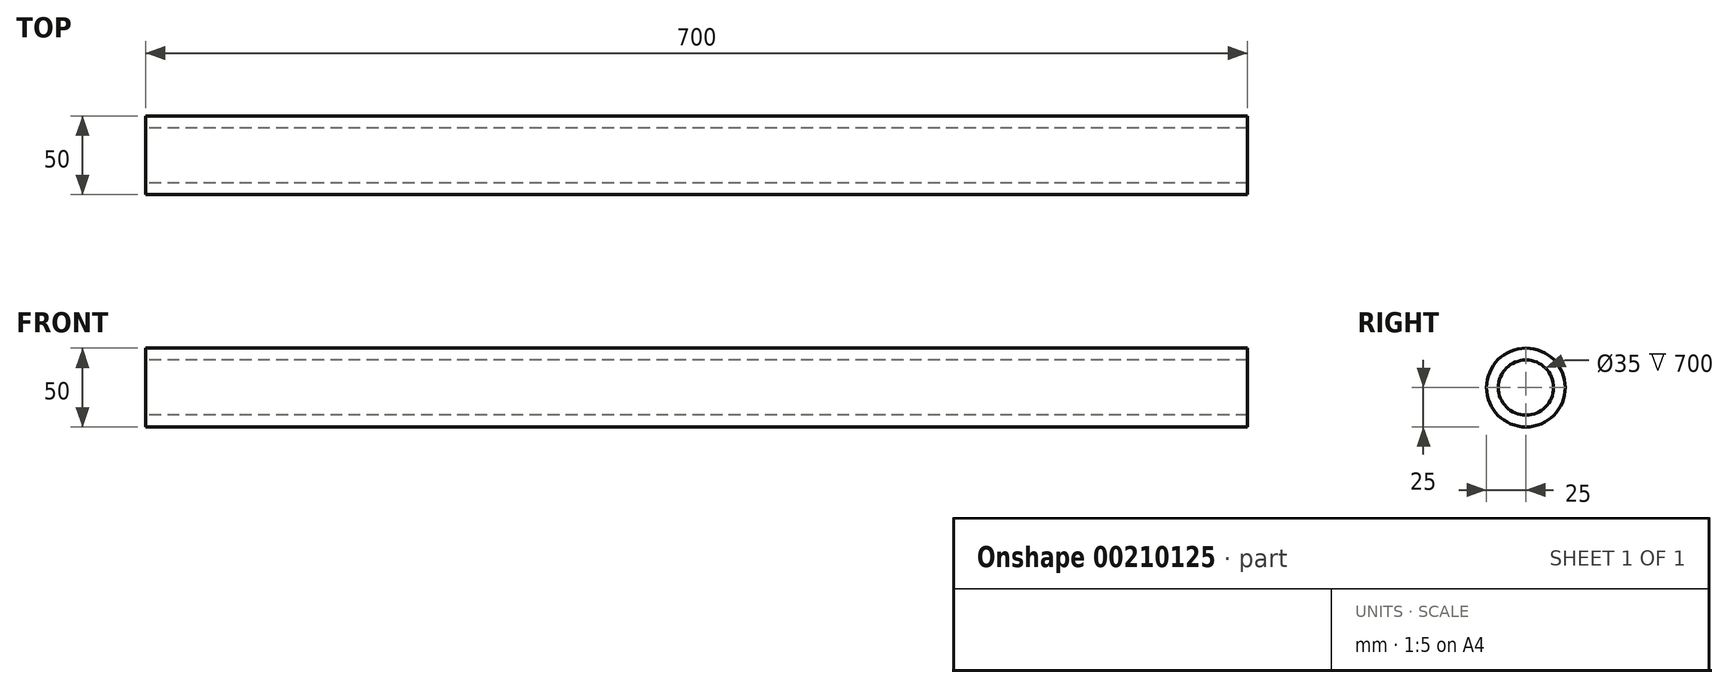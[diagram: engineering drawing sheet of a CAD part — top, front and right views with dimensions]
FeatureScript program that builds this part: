
annotation { "Feature Type Name" : "Feature", "Feature Type Description" : "" }
export const myFeature = defineFeature(function(context is Context, id is Id, definition is map)
    precondition{}
    {
        {
            var Q0;
            Q0=qCreatedBy(makeId("Right.planeOp"),FACE);
            var sketch = newSketch(context, id + "F0", { "sketchPlane" : qUnion([Q0])});
            skCircle(sketch, "E0", {"center": v(0, 0) * mm, "radius": 25 * mm});
            skCircle(sketch, "E1", {"center": v(0, 0) * mm, "radius": 17.5 * mm});
            skSolve(sketch);
        }
        {
            var Q0;
            Q0 = qSketchRegion(id + "F0", true);
            extrude(context, id + "F1", {"entities" : qUnion([Q0]), "depth" : 700 * mm});
        }
    });
